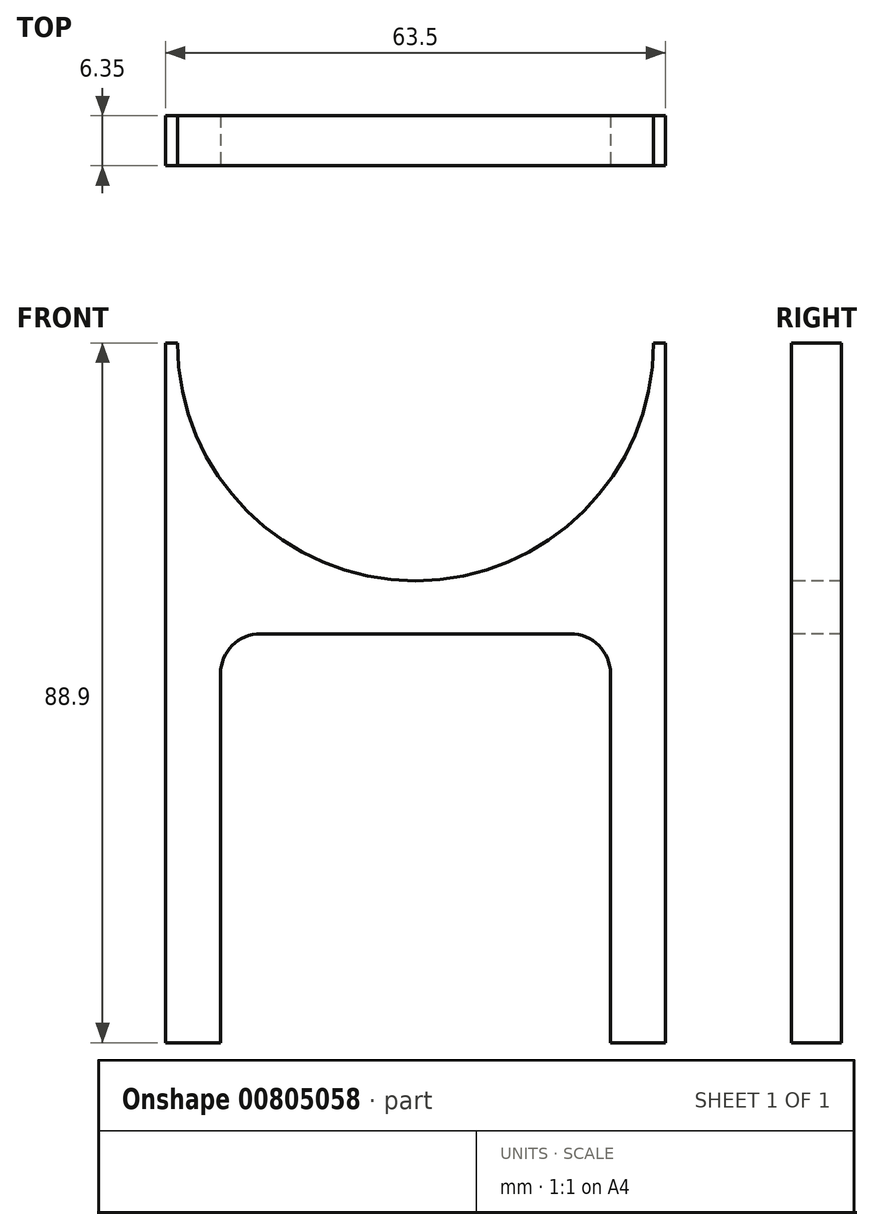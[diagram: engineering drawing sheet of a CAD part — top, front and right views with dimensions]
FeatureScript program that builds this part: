
annotation { "Feature Type Name" : "Feature", "Feature Type Description" : "" }
export const myFeature = defineFeature(function(context is Context, id is Id, definition is map)
    precondition{}
    {
        {
            var Q0;
            Q0=qCreatedBy(makeId("Front.planeOp"),FACE);
            var sketch = newSketch(context, id + "F0", { "sketchPlane" : qUnion([Q0])});
            skLineSegment(sketch, "E0.bottom", {"start": v(-31.75, 44.45) * mm, "end": v(31.75, 44.45) * mm});
            skLineSegment(sketch, "E0.top", {"start": v(-31.75, -44.45) * mm, "end": v(31.75, -44.45) * mm});
            skLineSegment(sketch, "E0.left", {"start": v(-31.75, 44.45) * mm, "end": v(-31.75, -44.45) * mm});
            skLineSegment(sketch, "E0.right", {"start": v(31.75, 44.45) * mm, "end": v(31.75, -44.45) * mm});
            skPoint(sketch, "E0.middle", {"position": v(0, 0) * mm});
            skSolve(sketch);
        }
        {
            var Q0;
            Q0 = qSketchRegion(id + "F0", true);
            extrude(context, id + "F1", {"entities" : qUnion([Q0]), "depth" : 6.35 * mm, "offsetDistance" : 25.4 * mm});
        }
        {
            var Q0;
            Q0=makeQuery(id+"F1.opExtrude","CAP_FACE",FACE,{"disambiguationData":[OSD([sQuery(id+"F0.wireOp",EDGE,"E0.bottom"),sQuery(id+"F0.wireOp",EDGE,"E0.top"),sQuery(id+"F0.wireOp",EDGE,"E0.left"),sQuery(id+"F0.wireOp",EDGE,"E0.right")])],"isStart":false});
            var sketch = newSketch(context, id + "F2", { "sketchPlane" : qUnion([Q0])});
            skCircle(sketch, "E1", {"center": v(0, 44.45) * mm, "radius": 30.23 * mm});
            skSolve(sketch);
        }
        {
            var Q0;
            Q0 = qSketchRegion(id + "F2", true);
            extrude(context, id + "F3", {"entities" : qUnion([Q0]), "operationType" : NewBodyOperationType.REMOVE, "endBound" : BoundingType.THROUGH_ALL, "oppositeDirection" : true, "depth" : 25.4 * mm, "offsetDistance" : 25.4 * mm});
        }
        {
            var Q0;
            Q0=makeQuery(id+"F1.opExtrude","CAP_FACE",FACE,{"disambiguationData":[OSD([sQuery(id+"F0.wireOp",EDGE,"E0.bottom"),sQuery(id+"F0.wireOp",EDGE,"E0.top"),sQuery(id+"F0.wireOp",EDGE,"E0.left"),sQuery(id+"F0.wireOp",EDGE,"E0.right")])],"isStart":false});
            var sketch = newSketch(context, id + "F4", { "sketchPlane" : qUnion([Q0])});
            skLineSegment(sketch, "E2.bottom", {"start": v(-24.77, -44.45) * mm, "end": v(24.76, -44.45) * mm});
            skLineSegment(sketch, "E2.top", {"start": v(-24.77, 7.5) * mm, "end": v(24.76, 7.5) * mm});
            skLineSegment(sketch, "E2.left", {"start": v(-24.77, -44.45) * mm, "end": v(-24.77, 7.5) * mm});
            skLineSegment(sketch, "E2.right", {"start": v(24.76, -44.45) * mm, "end": v(24.76, 7.5) * mm});
            skSolve(sketch);
        }
        {
            var Q0;
            Q0 = qSketchRegion(id + "F4", true);
            extrude(context, id + "F5", {"entities" : qUnion([Q0]), "operationType" : NewBodyOperationType.REMOVE, "endBound" : BoundingType.THROUGH_ALL, "oppositeDirection" : true, "depth" : 25.4 * mm, "offsetDistance" : 25.4 * mm});
        }
        {
            var Q0;
            Q0=makeQuery(id+"F5.boolean.opBoolean","COPY",EDGE,{"derivedFrom":makeQuery(id+"F5.opExtrude","SWEPT_EDGE",EDGE,{"disambiguationData":[OSD([sQuery(id+"F4.wireOp",EDGE,"E2.top"),sQuery(id+"F4.wireOp",EDGE,"E2.left")])]})});
            var Q1;
            Q1=makeQuery(id+"F5.boolean.opBoolean","COPY",EDGE,{"derivedFrom":makeQuery(id+"F5.opExtrude","SWEPT_EDGE",EDGE,{"disambiguationData":[OSD([sQuery(id+"F4.wireOp",EDGE,"E2.top"),sQuery(id+"F4.wireOp",EDGE,"E2.right")])]})});
            fillet(context, id + "F6", {"entities" : qUnion([Q0, Q1]), "radius" : 5.08 * mm, "tangentPropagation" : true, "allowEdgeOverflow" : false});
        }
    });
